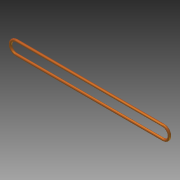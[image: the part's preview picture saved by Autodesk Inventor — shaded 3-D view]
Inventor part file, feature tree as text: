
AUTODESK INVENTOR PART (.ipt)
format: ipt  version: 2012 (Build 160160000, 160)  size: 82,944 bytes
history: native  units: in
note: dims shown in document units (in); Inventor stores cm internally (conversion verified against a paired STEP export)
features: sketch x2, sweep x1
ambient origin geometry x8: Origin, YZ Plane, XZ Plane, XY Plane, X Axis, Y Axis, Z Axis, Center Point
bodies: Solid1 (feature_tree)
feature tree (3):
  sweep  "Sweep1"
  sketch  "Sketch1"  dims[d0=15.125in d1=0.625in]
  sketch  "Sketch2"  dims[d2=0.625in d3=0.25in d4=0.0in]
